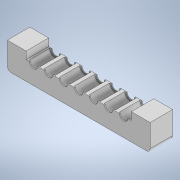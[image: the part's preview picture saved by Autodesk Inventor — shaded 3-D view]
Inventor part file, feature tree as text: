
AUTODESK INVENTOR PART (.ipt)
format: ipt  version: 2021 (Build 250183000, 183)  size: 211,456 bytes
history: native  units: mm
features: extrude x5, sketch x5, fillet x1
ambient origin geometry x8: Origin, YZ Plane, XZ Plane, XY Plane, X Axis, Y Axis, Z Axis, Center Point
bodies: Solid1 (feature_tree)
feature tree (11):
  extrude  "Extrusion1"  Depth=56.0mm
  extrude  "Extrusion2"  Depth=10.0mm
  extrude  "Extrusion3"  Depth=10.0mm
  extrude  "Extrusion4"  Depth=6.0mm
  extrude  "Extrusion5"  Depth=4.0mm
  fillet  "Fillet1"  Radius=10.0mm
  sketch  "Sketch1"  dims[d2=56.0mm d3=8.0mm]
  sketch  "Sketch2"  dims[d4=10.0mm d5=10.0mm]
  sketch  "Sketch3"  dims[d6=10.0mm d7=10.0mm]
  sketch  "Sketch4"  dims[d8=6.0mm d9=6.0mm]
  sketch  "Sketch5"  dims[d10=4.0mm d11=4.0mm d12=70.0mm d14=8.0mm d15=10.0mm d17=10.0mm d19=11.0mm d20=0.0mm d21=0.5mm d22=0.0mm d23=0.5mm d24=0.0mm d27=4.0mm d28=56.0mm d29=100.0mm d30=0.0mm d31=4.5mm d32=70.0mm d34=8.0mm d35=10.0mm d37=10.0mm d39=100.0mm d40=0.0mm d41=2.0mm]
